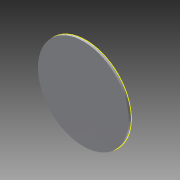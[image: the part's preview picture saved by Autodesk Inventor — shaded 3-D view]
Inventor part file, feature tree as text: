
AUTODESK INVENTOR PART (.ipt)
format: ipt  version: 2014 (Build 180170000, 170)  size: 268,288 bytes
history: native  units: mm
features: sketch x6, extrude x5, fillet x1
ambient origin geometry x8: Origin, YZ Plane, XZ Plane, XY Plane, X Axis, Y Axis, Z Axis, Center Point
bodies: Solid1 (feature_tree)
feature tree (12):
  extrude  "Extrusion1"  Depth=2.0mm TaperAngle=0.0deg
  extrude  "Extrusion2"  Depth=60.0mm TaperAngle=360.0deg
  extrude  "Extrusion3"  Depth=50.0mm
  extrude  "Extrusion4"  Depth=50.0mm
  fillet  "Fillet1"  Radius=50.0mm
  sketch  "Sketch5"  dims[d26=50.0mm d28=70.0mm]
  extrude  "Extrusion5"  Depth=70.0mm
  sketch  "Sketch1"  dims[d0=155.0mm d4=2.0mm d5=0.0mm]
  sketch  "Sketch2"  dims[d15=0.436332mm d16=60.0mm d18=360.0deg]
  sketch  "Sketch3"  dims[d21=50.0mm d22=50.0mm]
  sketch  "Sketch4"  dims[d23=50.0mm d24=50.0mm d25=50.0mm]
  sketch  "Sketch6"  dims[d29=70.0mm d30=70.0mm d31=70.0mm d32=70.0mm d33=70.0mm d34=5.0mm d35=2.0mm d36=0.0mm d37=12.8mm d38=6.6mm d39=0.0mm d40=4.4mm d41=12.0mm d42=0.0mm d43=5.0mm d44=79.0mm d45=75.0mm d46=1.0mm d47=0.0mm]
